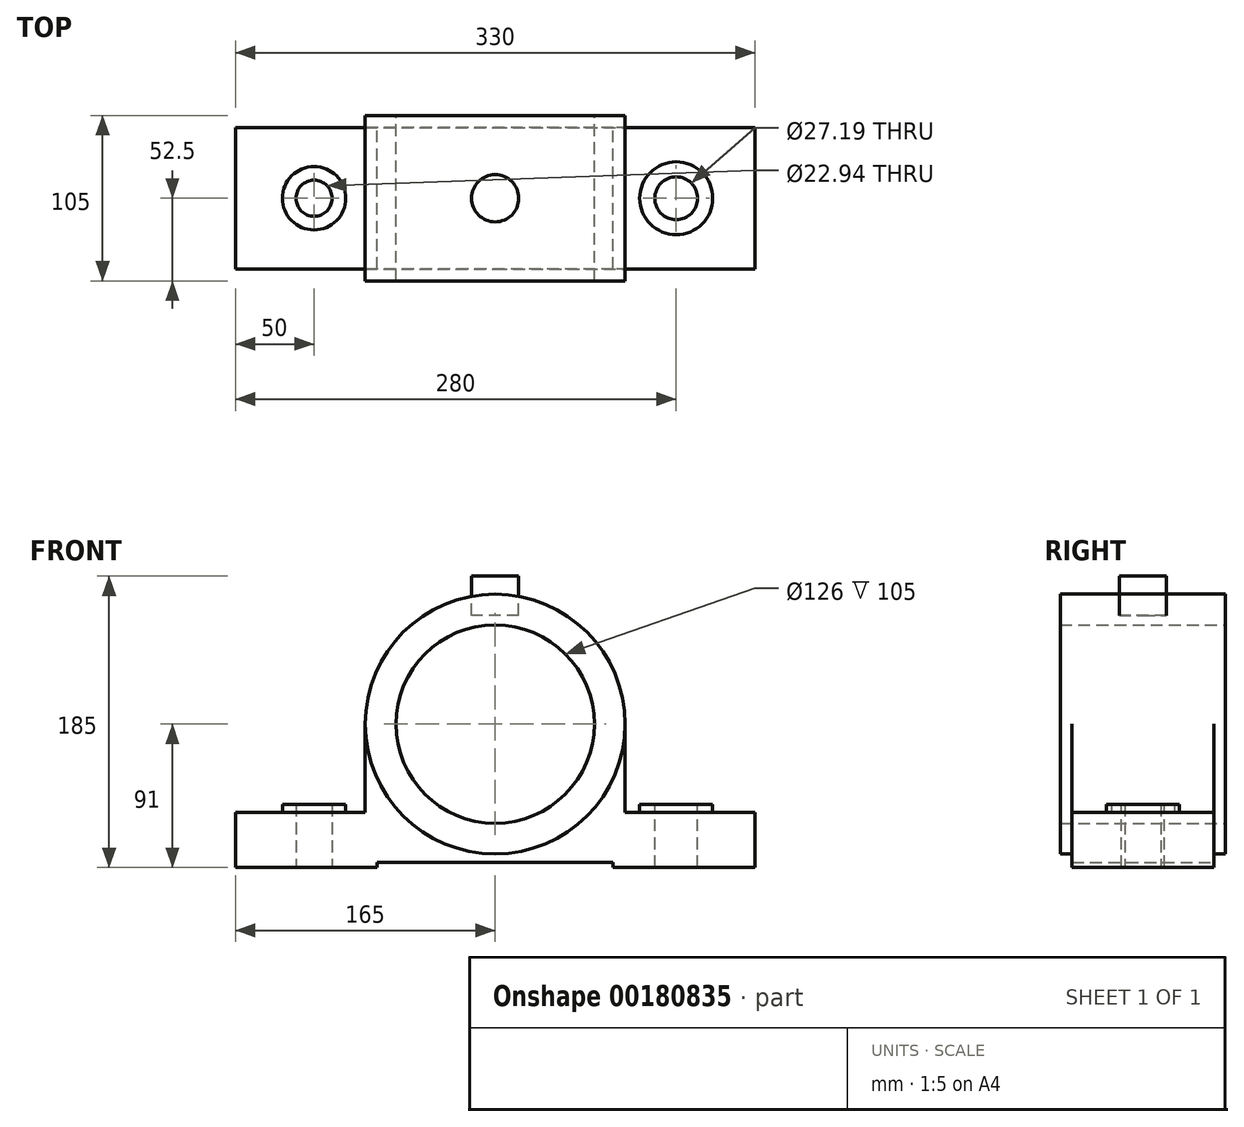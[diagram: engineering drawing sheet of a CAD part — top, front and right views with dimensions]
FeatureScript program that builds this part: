
annotation { "Feature Type Name" : "Feature", "Feature Type Description" : "" }
export const myFeature = defineFeature(function(context is Context, id is Id, definition is map)
    precondition{}
    {
        {
            var Q0;
            Q0=qCreatedBy(makeId("Front.planeOp"),FACE);
            var sketch = newSketch(context, id + "F0", { "sketchPlane" : qUnion([Q0])});
            skLineSegment(sketch, "E0", {"start": v(0, 0) * mm, "end": v(-165, 0) * mm});
            skLineSegment(sketch, "E1", {"start": v(-165, 0) * mm, "end": v(-165, 35) * mm});
            skLineSegment(sketch, "E2", {"start": v(-165, 35) * mm, "end": v(-82.5, 35) * mm});
            skLineSegment(sketch, "E3", {"start": v(-82.5, 35) * mm, "end": v(-82.5, 91) * mm});
            skLineSegment(sketch, "E4", {"start": v(82.5, 91) * mm, "end": v(82.5, 35) * mm});
            skLineSegment(sketch, "E5", {"start": v(82.5, 35) * mm, "end": v(165, 35) * mm});
            skLineSegment(sketch, "E6", {"start": v(165, 35) * mm, "end": v(165, 0) * mm});
            skLineSegment(sketch, "E7", {"start": v(165, 0) * mm, "end": v(0, 0) * mm});
            skCircle(sketch, "E8", {"center": v(0, 91) * mm, "radius": 82.5 * mm});
            skCircle(sketch, "E9", {"center": v(0, 91) * mm, "radius": 63 * mm});
            skSolve(sketch);
        }
        {
            var Q0;
            Q0=makeQuery(id+"F0.imprint","IMPRINT",FACE,{"disambiguationData":[TD([[makeQuery(id+"F0.imprint","IMPRINT",EDGE,{"derivedFrom":sQuery(id+"F0.wireOp",EDGE,"E9")}),-1.0]])]});
            extrude(context, id + "F1", {"entities" : qUnion([Q0]), "endBound" : BoundingType.SYMMETRIC, "depth" : 105 * mm});
        }
        {
            var Q0;
            Q0 = qSketchRegion(id + "F0", true);
            extrude(context, id + "F2", {"entities" : qUnion([Q0]), "operationType" : NewBodyOperationType.ADD, "endBound" : BoundingType.SYMMETRIC, "depth" : 90 * mm});
        }
        {
            var Q0;
            Q0=makeQuery(id+"F2.opExtrude","SWEPT_FACE",FACE,{"disambiguationData":[OSD([sQuery(id+"F0.wireOp",EDGE,"E2")])]});
            var sketch = newSketch(context, id + "F3", { "sketchPlane" : qUnion([Q0])});
            skCircle(sketch, "E10", {"center": v(-115, 0) * mm, "radius": 20.13 * mm});
            skCircle(sketch, "E11", {"center": v(115, 0) * mm, "radius": 23.17 * mm});
            skCircle(sketch, "E12", {"center": v(115, 0) * mm, "radius": 13.6 * mm});
            skCircle(sketch, "E13", {"center": v(-115, 0) * mm, "radius": 11.47 * mm});
            skSolve(sketch);
        }
        {
            var Q0;
            Q0=makeQuery(id+"F3.imprint","IMPRINT",FACE,{"disambiguationData":[TD([[makeQuery(id+"F3.imprint","IMPRINT",EDGE,{"derivedFrom":sQuery(id+"F3.wireOp",EDGE,"E12")}),1.0]])]});
            extrude(context, id + "F4", {"entities" : qUnion([Q0]), "operationType" : NewBodyOperationType.REMOVE, "oppositeDirection" : true, "depth" : 50 * mm});
        }
        {
            var Q0;
            Q0 = qSketchRegion(id + "F3", true);
            extrude(context, id + "F5", {"entities" : qUnion([Q0]), "operationType" : NewBodyOperationType.ADD, "depth" : 5 * mm});
        }
        {
            var Q0;
            Q0=makeQuery(id+"F5.boolean.opBoolean","SPLIT",FACE,{"disambiguationData":[TD([makeQuery(id+"F5.opExtrude","SWEPT_FACE",FACE,{"disambiguationData":[OSD([sQuery(id+"F3.wireOp",EDGE,"E13")])]})])],"derivedFrom":makeQuery(id+"F2.opExtrude","SWEPT_FACE",FACE,{"disambiguationData":[OSD([sQuery(id+"F0.wireOp",EDGE,"E2")])]})});
            extrude(context, id + "F6", {"entities" : qUnion([Q0]), "operationType" : NewBodyOperationType.REMOVE, "oppositeDirection" : true, "depth" : 50 * mm});
        }
        {
            var Q0;
            Q0=makeQuery(id+"F2.opExtrude","SWEPT_FACE",FACE,{"disambiguationData":[OSD([sQuery(id+"F0.wireOp",EDGE,"E0"),sQuery(id+"F0.wireOp",EDGE,"E7")])]});
            var sketch = newSketch(context, id + "F7", { "sketchPlane" : qUnion([Q0])});
            skLineSegment(sketch, "E14.bottom", {"start": v(75, 45) * mm, "end": v(-75, 45) * mm});
            skLineSegment(sketch, "E14.top", {"start": v(75, -45) * mm, "end": v(-75, -45) * mm});
            skLineSegment(sketch, "E14.left", {"start": v(75, 45) * mm, "end": v(75, -45) * mm});
            skLineSegment(sketch, "E14.right", {"start": v(-75, 45) * mm, "end": v(-75, -45) * mm});
            skPoint(sketch, "E14.middle", {"position": v(0, 0) * mm});
            skSolve(sketch);
        }
        {
            var Q0;
            Q0 = qSketchRegion(id + "F7", true);
            extrude(context, id + "F8", {"entities" : qUnion([Q0]), "operationType" : NewBodyOperationType.REMOVE, "oppositeDirection" : true, "depth" : 3 * mm});
        }
        {
            var Q0;
            Q0=qCreatedBy(makeId("Top.planeOp"),FACE);
            cPlane(context, id + "F9", {"entities" : qUnion([Q0]), "cplaneType" : CPlaneType.OFFSET, "offset" : 185 * mm, "width" : 150 * mm, "height" : 150 * mm});
        }
        {
            var Q0;
            Q0=qCreatedBy(id+"F9.planeOp",FACE);
            var sketch = newSketch(context, id + "F10", { "sketchPlane" : qUnion([Q0])});
            skCircle(sketch, "E15", {"center": v(0, 0) * mm, "radius": 15 * mm});
            skSolve(sketch);
        }
        {
            var Q0;
            Q0 = qSketchRegion(id + "F10", true);
            extrude(context, id + "F11", {"entities" : qUnion([Q0]), "oppositeDirection" : true, "depth" : 25 * mm});
        }
    });
